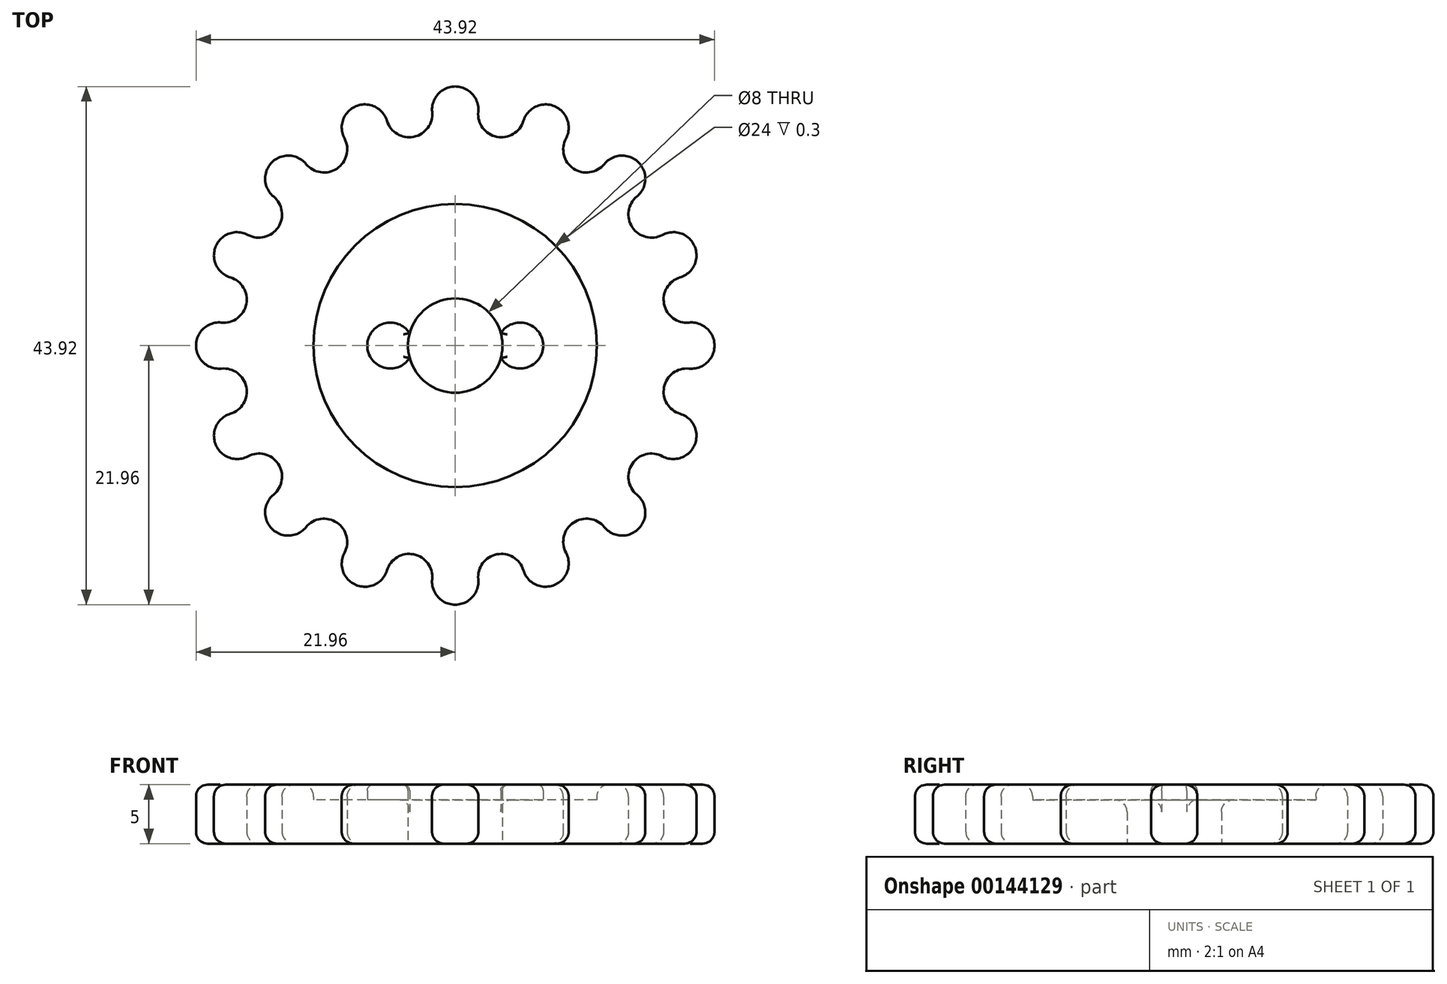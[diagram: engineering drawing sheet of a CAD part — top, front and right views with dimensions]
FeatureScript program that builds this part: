
annotation { "Feature Type Name" : "Feature", "Feature Type Description" : "" }
export const myFeature = defineFeature(function(context is Context, id is Id, definition is map)
    precondition{}
    {
        {
            var Q0;
            Q0=qCreatedBy(makeId("Top.planeOp"),FACE);
            var sketch = newSketch(context, id + "F0", { "sketchPlane" : qUnion([Q0])});
            skCircle(sketch, "E0", {"center": v(0, 0) * mm, "radius": 12 * mm});
            skCircle(sketch, "E1", {"center": v(0, 0) * mm, "radius": 20 * mm, "construction": true});
            skCircle(sketch, "E2", {"center": v(0, 0) * mm, "radius": 4 * mm});
            skCircle(sketch, "E3", {"center": v(5.5, 0) * mm, "radius": 1.95 * mm});
            skCircle(sketch, "E4", {"center": v(0, 0) * mm, "radius": 5.5 * mm, "construction": true});
            skCircle(sketch, "E5", {"center": v(-5.5, 0) * mm, "radius": 1.95 * mm});
            skArc(sketch, "E6", {"start": v(19.8, -1.95) * mm, "mid": v(21.96, 0) * mm, "end": v(19.8, 1.95) * mm});
            skArc(sketch, "E7", {"start": v(19.8, -1.95) * mm, "mid": v(17.7, -3.52) * mm, "end": v(19.05, -5.78) * mm});
            skArc(sketch, "E8", {"start": v(17.55, -9.38) * mm, "mid": v(20.29, -8.4) * mm, "end": v(19.05, -5.78) * mm});
            skArc(sketch, "E9", {"start": v(17.55, -9.38) * mm, "mid": v(15, -10.02) * mm, "end": v(15.39, -12.63) * mm});
            skArc(sketch, "E10", {"start": v(12.63, -15.39) * mm, "mid": v(15.53, -15.53) * mm, "end": v(15.39, -12.63) * mm});
            skArc(sketch, "E11", {"start": v(12.63, -15.39) * mm, "mid": v(10.02, -15) * mm, "end": v(9.38, -17.55) * mm});
            skArc(sketch, "E12", {"start": v(5.78, -19.05) * mm, "mid": v(8.4, -20.29) * mm, "end": v(9.38, -17.55) * mm});
            skArc(sketch, "E13", {"start": v(5.78, -19.05) * mm, "mid": v(3.52, -17.7) * mm, "end": v(1.95, -19.8) * mm});
            skArc(sketch, "E14", {"start": v(-1.95, -19.8) * mm, "mid": v(0, -21.96) * mm, "end": v(1.95, -19.8) * mm});
            skArc(sketch, "E15", {"start": v(-1.95, -19.8) * mm, "mid": v(-3.52, -17.7) * mm, "end": v(-5.78, -19.05) * mm});
            skArc(sketch, "E16", {"start": v(-9.38, -17.55) * mm, "mid": v(-8.4, -20.29) * mm, "end": v(-5.78, -19.05) * mm});
            skArc(sketch, "E17", {"start": v(-9.38, -17.55) * mm, "mid": v(-10.02, -15) * mm, "end": v(-12.63, -15.39) * mm});
            skArc(sketch, "E18", {"start": v(-15.39, -12.63) * mm, "mid": v(-15.53, -15.53) * mm, "end": v(-12.63, -15.39) * mm});
            skArc(sketch, "E19", {"start": v(-15.39, -12.63) * mm, "mid": v(-15, -10.02) * mm, "end": v(-17.55, -9.38) * mm});
            skArc(sketch, "E20", {"start": v(-19.05, -5.78) * mm, "mid": v(-20.29, -8.4) * mm, "end": v(-17.55, -9.38) * mm});
            skArc(sketch, "E21", {"start": v(-19.05, -5.78) * mm, "mid": v(-17.7, -3.52) * mm, "end": v(-19.8, -1.95) * mm});
            skArc(sketch, "E22", {"start": v(-19.8, 1.95) * mm, "mid": v(-21.96, 0) * mm, "end": v(-19.8, -1.95) * mm});
            skArc(sketch, "E23", {"start": v(-19.8, 1.95) * mm, "mid": v(-17.7, 3.52) * mm, "end": v(-19.05, 5.78) * mm});
            skArc(sketch, "E24", {"start": v(-17.55, 9.38) * mm, "mid": v(-20.29, 8.4) * mm, "end": v(-19.05, 5.78) * mm});
            skArc(sketch, "E25", {"start": v(-17.55, 9.38) * mm, "mid": v(-15, 10.02) * mm, "end": v(-15.39, 12.63) * mm});
            skArc(sketch, "E26", {"start": v(9.38, 17.55) * mm, "mid": v(8.4, 20.29) * mm, "end": v(5.78, 19.05) * mm});
            skArc(sketch, "E27", {"start": v(9.38, 17.55) * mm, "mid": v(10.02, 15) * mm, "end": v(12.63, 15.39) * mm});
            skArc(sketch, "E28", {"start": v(15.39, 12.63) * mm, "mid": v(15.53, 15.53) * mm, "end": v(12.63, 15.39) * mm});
            skArc(sketch, "E29", {"start": v(15.39, 12.63) * mm, "mid": v(15, 10.02) * mm, "end": v(17.55, 9.38) * mm});
            skArc(sketch, "E30", {"start": v(19.05, 5.78) * mm, "mid": v(20.29, 8.4) * mm, "end": v(17.55, 9.38) * mm});
            skArc(sketch, "E31", {"start": v(19.05, 5.78) * mm, "mid": v(17.7, 3.52) * mm, "end": v(19.8, 1.95) * mm});
            skArc(sketch, "E32", {"start": v(-12.63, 15.39) * mm, "mid": v(-10.02, 15) * mm, "end": v(-9.38, 17.55) * mm});
            skArc(sketch, "E33", {"start": v(-12.63, 15.39) * mm, "mid": v(-15.53, 15.53) * mm, "end": v(-15.39, 12.63) * mm});
            skArc(sketch, "E34", {"start": v(-5.78, 19.05) * mm, "mid": v(-8.4, 20.29) * mm, "end": v(-9.38, 17.55) * mm});
            skArc(sketch, "E35", {"start": v(-5.78, 19.05) * mm, "mid": v(-3.52, 17.7) * mm, "end": v(-1.95, 19.8) * mm});
            skArc(sketch, "E36", {"start": v(1.95, 19.8) * mm, "mid": v(0, 21.96) * mm, "end": v(-1.95, 19.8) * mm});
            skArc(sketch, "E37", {"start": v(1.95, 19.8) * mm, "mid": v(3.52, 17.7) * mm, "end": v(5.78, 19.05) * mm});
            skSolve(sketch);
        }
        {
            var Q0;
            Q0=makeQuery(id+"F0.imprint","IMPRINT",FACE,{"disambiguationData":[TD([[makeQuery(id+"F0.imprint","IMPRINT",EDGE,{"derivedFrom":sQuery(id+"F0.wireOp",EDGE,"E0")}),1.0]])]});
            extrude(context, id + "F1", {"entities" : qUnion([Q0]), "depth" : 3.7 * mm});
        }
        {
            var Q0;
            Q0=makeQuery(id+"F0.imprint","IMPRINT",FACE,{"disambiguationData":[TD([[makeQuery(id+"F0.imprint","IMPRINT",EDGE,{"derivedFrom":sQuery(id+"F0.wireOp",EDGE,"E0")}),-1.0]])]});
            var Q1;
            Q1=makeQuery(id+"F0.imprint","IMPRINT",FACE,{"disambiguationData":[TD([[makeQuery(id+"F0.imprint","IMPRINT",EDGE,{"derivedFrom":sQuery(id+"F0.wireOp",EDGE,"E5")}),1.0]])]});
            var Q2;
            Q2=makeQuery(id+"F0.imprint","IMPRINT",FACE,{"disambiguationData":[TD([[makeQuery(id+"F0.imprint","IMPRINT",EDGE,{"derivedFrom":sQuery(id+"F0.wireOp",EDGE,"E3")}),1.0]])]});
            extrude(context, id + "F2", {"entities" : qUnion([Q0, Q1, Q2]), "operationType" : NewBodyOperationType.ADD, "depth" : 5 * mm});
        }
        {
            var Q0;
            {var subQ0=sQuery(id+"F0.wireOp",EDGE,"E5");var subQ1=sQuery(id+"F0.wireOp",EDGE,"E2");var subQ2=makeQuery(id+"F0.imprint","INTERSECT",VERTEX,{"disambiguationData":[OD(0.0)],"derivedFrom":[subQ1,subQ0]});Q0=makeQuery(id+"F0.imprint","IMPRINT",FACE,{"disambiguationData":[TD([[makeQuery(id+"F0.imprint","IMPRINT",EDGE,{"disambiguationData":[TD([[subQ2,-1.0]])],"derivedFrom":subQ1}),1.0]])]});}
            var Q1;
            {var subQ0=sQuery(id+"F0.wireOp",EDGE,"E3");var subQ1=sQuery(id+"F0.wireOp",EDGE,"E2");var subQ2=makeQuery(id+"F0.imprint","INTERSECT",VERTEX,{"disambiguationData":[OD(0.0)],"derivedFrom":[subQ1,subQ0]});Q1=makeQuery(id+"F0.imprint","IMPRINT",FACE,{"disambiguationData":[TD([[makeQuery(id+"F0.imprint","IMPRINT",EDGE,{"disambiguationData":[TD([[subQ2,1.0]])],"derivedFrom":subQ1}),1.0]])]});}
            extrude(context, id + "F3", {"entities" : qUnion([Q0, Q1]), "operationType" : NewBodyOperationType.REMOVE, "depth" : 25 * mm});
        }
        {
            var Q0;
            Q0=makeQuery(id+"F2.opExtrude","CAP_EDGE",EDGE,{"disambiguationData":[OSD([sQuery(id+"F0.wireOp",EDGE,"E23")])],"isStart":false});
            var Q1;
            Q1=makeQuery(id+"F2.opExtrude","CAP_EDGE",EDGE,{"disambiguationData":[OSD([sQuery(id+"F0.wireOp",EDGE,"E0")])],"isStart":false});
            var Q2;
            Q2=makeQuery(id+"F1.opExtrude","CAP_EDGE",EDGE,{"disambiguationData":[OSD([sQuery(id+"F0.wireOp",EDGE,"E2")])],"isStart":false});
            var Q3;
            Q3=makeQuery(id+"F2.opExtrude","CAP_EDGE",EDGE,{"disambiguationData":[OSD([sQuery(id+"F0.wireOp",EDGE,"E16")])],"isStart":true});
            var Q4;
            Q4=makeQuery(id+"F1.opExtrude","CAP_EDGE",EDGE,{"disambiguationData":[OSD([sQuery(id+"F0.wireOp",EDGE,"E2")])],"isStart":true});
            fillet(context, id + "F4", {"entities" : qUnion([Q0, Q1, Q2, Q3, Q4]), "radius" : 1 * mm, "tangentPropagation" : true, "allowEdgeOverflow" : false});
        }
        {
            var Q0;
            Q0=makeQuery(id+"F2.opExtrude","CAP_EDGE",EDGE,{"disambiguationData":[OSD([sQuery(id+"F0.wireOp",EDGE,"E5")])],"isStart":false});
            var Q1;
            Q1=makeQuery(id+"F2.opExtrude","CAP_EDGE",EDGE,{"disambiguationData":[OSD([sQuery(id+"F0.wireOp",EDGE,"E3")])],"isStart":false});
            var Q2;
            {var subQ0=sQuery(id+"F0.wireOp",EDGE,"E3");var subQ1=sQuery(id+"F0.wireOp",EDGE,"E2");Q2=makeQuery(id+"F3.boolean.opBoolean","INTERSECT",EDGE,{"derivedFrom":[makeQuery(id+"F2.opExtrude","CAP_FACE",FACE,{"disambiguationData":[OSD([subQ0])],"isStart":false}),makeQuery(id+"F3.opExtrude","SWEPT_FACE",FACE,{"disambiguationData":[OSD([subQ1]),TDD([makeQuery(id+"F0.imprint","IMPRINT",EDGE,{"disambiguationData":[TD([[makeQuery(id+"F0.imprint","INTERSECT",VERTEX,{"disambiguationData":[OD(0.0)],"derivedFrom":[subQ1,subQ0]}),1.0]])],"derivedFrom":subQ1})])]})]});}
            var Q3;
            {var subQ0=sQuery(id+"F0.wireOp",EDGE,"E3");var subQ1=sQuery(id+"F0.wireOp",EDGE,"E2");Q3=makeQuery(id+"F3.boolean.opBoolean","COPY",EDGE,{"derivedFrom":makeQuery(id+"F3.opExtrude","SWEPT_EDGE",EDGE,{"disambiguationData":[OSD([subQ1,subQ0]),TDD([makeQuery(id+"F0.imprint","INTERSECT",VERTEX,{"disambiguationData":[OD(0.0)],"derivedFrom":[subQ1,subQ0]})])]})});}
            var Q4;
            {var subQ0=sQuery(id+"F0.wireOp",EDGE,"E3");var subQ1=sQuery(id+"F0.wireOp",EDGE,"E2");Q4=makeQuery(id+"F3.boolean.opBoolean","COPY",EDGE,{"derivedFrom":makeQuery(id+"F3.opExtrude","SWEPT_EDGE",EDGE,{"disambiguationData":[OSD([subQ1,subQ0]),TDD([makeQuery(id+"F0.imprint","INTERSECT",VERTEX,{"disambiguationData":[OD(1.0)],"derivedFrom":[subQ1,subQ0]})])]})});}
            var Q5;
            {var subQ0=sQuery(id+"F0.wireOp",EDGE,"E5");var subQ1=sQuery(id+"F0.wireOp",EDGE,"E2");Q5=makeQuery(id+"F3.boolean.opBoolean","COPY",EDGE,{"derivedFrom":makeQuery(id+"F3.opExtrude","SWEPT_EDGE",EDGE,{"disambiguationData":[OSD([subQ1,subQ0]),TDD([makeQuery(id+"F0.imprint","INTERSECT",VERTEX,{"disambiguationData":[OD(0.0)],"derivedFrom":[subQ1,subQ0]})])]})});}
            var Q6;
            {var subQ0=sQuery(id+"F0.wireOp",EDGE,"E5");var subQ1=sQuery(id+"F0.wireOp",EDGE,"E2");Q6=makeQuery(id+"F3.boolean.opBoolean","INTERSECT",EDGE,{"derivedFrom":[makeQuery(id+"F2.opExtrude","CAP_FACE",FACE,{"disambiguationData":[OSD([subQ0])],"isStart":false}),makeQuery(id+"F3.opExtrude","SWEPT_FACE",FACE,{"disambiguationData":[OSD([subQ1]),TDD([makeQuery(id+"F0.imprint","IMPRINT",EDGE,{"disambiguationData":[TD([[makeQuery(id+"F0.imprint","INTERSECT",VERTEX,{"disambiguationData":[OD(0.0)],"derivedFrom":[subQ1,subQ0]}),-1.0]])],"derivedFrom":subQ1})])]})]});}
            var Q7;
            {var subQ0=sQuery(id+"F0.wireOp",EDGE,"E5");var subQ1=sQuery(id+"F0.wireOp",EDGE,"E2");Q7=makeQuery(id+"F3.boolean.opBoolean","COPY",EDGE,{"derivedFrom":makeQuery(id+"F3.opExtrude","SWEPT_EDGE",EDGE,{"disambiguationData":[OSD([subQ1,subQ0]),TDD([makeQuery(id+"F0.imprint","INTERSECT",VERTEX,{"disambiguationData":[OD(1.0)],"derivedFrom":[subQ1,subQ0]})])]})});}
            fillet(context, id + "F5", {"entities" : qUnion([Q0, Q1, Q2, Q3, Q4, Q5, Q6, Q7]), "radius" : 0.5 * mm, "tangentPropagation" : true, "allowEdgeOverflow" : false});
        }
    });
